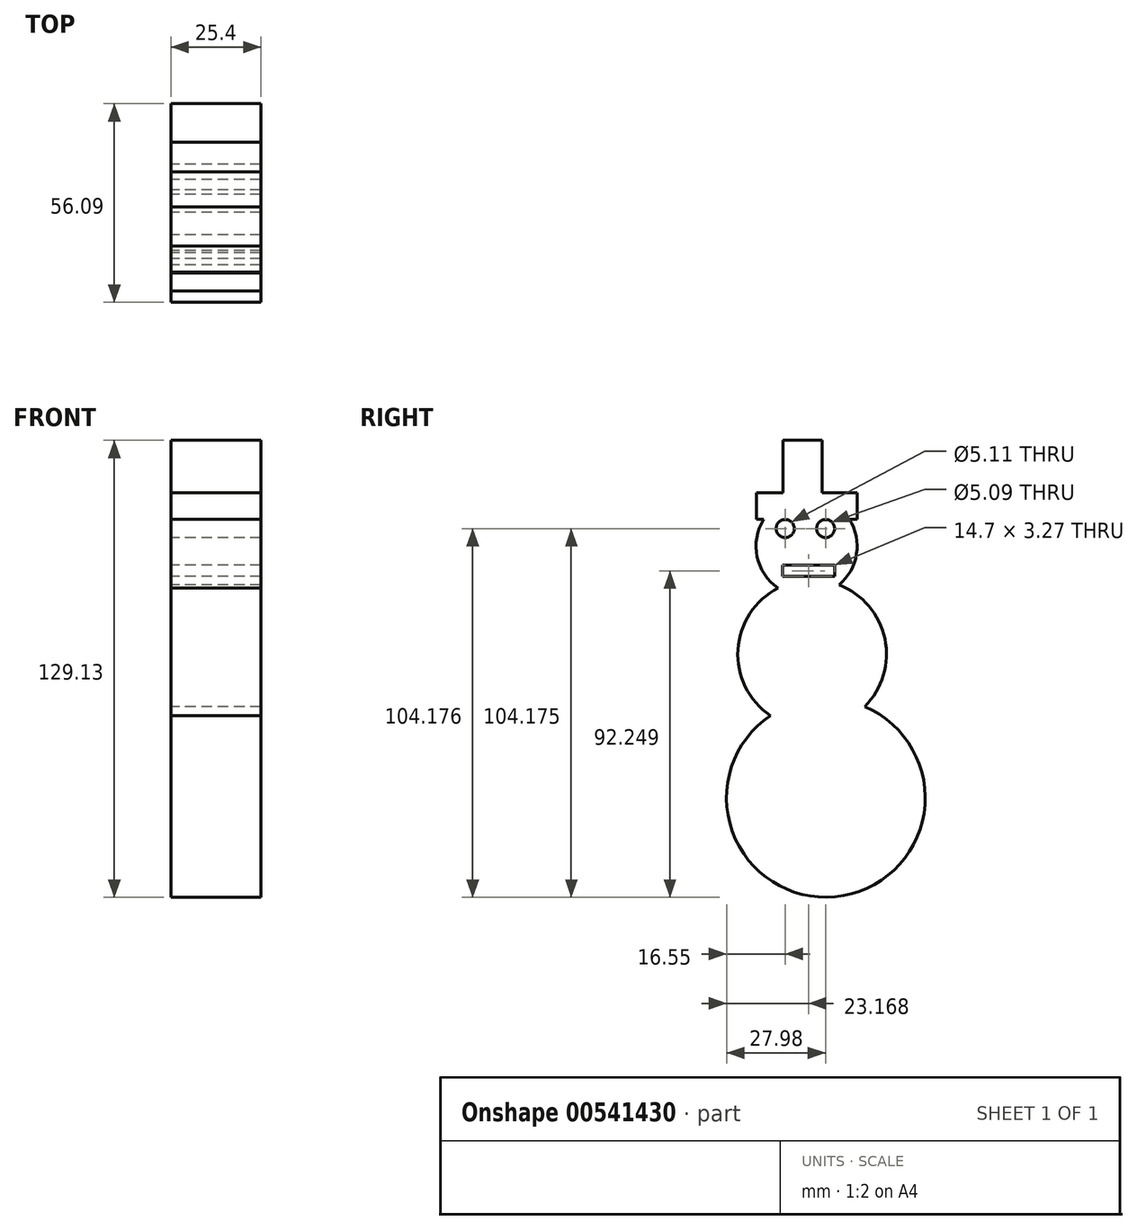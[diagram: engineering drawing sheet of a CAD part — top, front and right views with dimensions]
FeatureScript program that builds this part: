
annotation { "Feature Type Name" : "Feature", "Feature Type Description" : "" }
export const myFeature = defineFeature(function(context is Context, id is Id, definition is map)
    precondition{}
    {
        {
            var Q0;
            Q0=qCreatedBy(makeId("Right.planeOp"),FACE);
            var sketch = newSketch(context, id + "F0", { "sketchPlane" : qUnion([Q0])});
            skCircle(sketch, "E0", {"center": v(-8.83, -44.63) * mm, "radius": 28.05 * mm});
            skCircle(sketch, "E1", {"center": v(-12.7, -4) * mm, "radius": 21 * mm});
            skCircle(sketch, "E2", {"center": v(-14.27, 26.49) * mm, "radius": 14.27 * mm});
            skLineSegment(sketch, "E3.bottom", {"start": v(-28.42, 41.56) * mm, "end": v(0, 41.56) * mm});
            skLineSegment(sketch, "E3.top", {"start": v(-28.42, 34.1) * mm, "end": v(0, 34.1) * mm});
            skLineSegment(sketch, "E3.left", {"start": v(-28.42, 41.56) * mm, "end": v(-28.42, 34.1) * mm});
            skLineSegment(sketch, "E3.right", {"start": v(0, 41.56) * mm, "end": v(0, 34.1) * mm});
            skLineSegment(sketch, "E4.bottom", {"start": v(-20.97, 56.45) * mm, "end": v(-9.93, 56.45) * mm});
            skLineSegment(sketch, "E4.top", {"start": v(-20.97, 41.56) * mm, "end": v(-9.93, 41.56) * mm});
            skLineSegment(sketch, "E4.left", {"start": v(-20.97, 56.45) * mm, "end": v(-20.97, 41.56) * mm});
            skLineSegment(sketch, "E4.right", {"start": v(-9.93, 56.45) * mm, "end": v(-9.93, 41.56) * mm});
            skSolve(sketch);
        }
        {
            var Q0;
            Q0 = qSketchRegion(id + "F0", true);
            extrude(context, id + "F1", {"entities" : qUnion([Q0]), "depth" : 25.4 * mm, "offsetDistance" : 25.4 * mm});
        }
        {
            var Q0;
            Q0 = qSketchRegion(id + "F0", true);
            extrude(context, id + "F2", {"entities" : qUnion([Q0]), "operationType" : NewBodyOperationType.ADD, "depth" : 25.4 * mm, "offsetDistance" : 25.4 * mm});
        }
        {
            var Q0;
            Q0=qCreatedBy(makeId("Right.planeOp"),FACE);
            var sketch = newSketch(context, id + "F3", { "sketchPlane" : qUnion([Q0])});
            skCircle(sketch, "E5", {"center": v(-20.32, 31.5) * mm, "radius": 2.56 * mm});
            skCircle(sketch, "E6", {"center": v(-8.9, 31.5) * mm, "radius": 2.54 * mm});
            skLineSegment(sketch, "E7.bottom", {"start": v(-21.05, 21.2) * mm, "end": v(-6.35, 21.2) * mm});
            skLineSegment(sketch, "E7.top", {"start": v(-21.05, 17.94) * mm, "end": v(-6.35, 17.94) * mm});
            skLineSegment(sketch, "E7.left", {"start": v(-21.05, 21.2) * mm, "end": v(-21.05, 17.94) * mm});
            skLineSegment(sketch, "E7.right", {"start": v(-6.35, 21.2) * mm, "end": v(-6.35, 17.94) * mm});
            skSolve(sketch);
        }
        {
            var Q0;
            Q0 = qSketchRegion(id + "F3", true);
            extrude(context, id + "F4", {"entities" : qUnion([Q0]), "operationType" : NewBodyOperationType.REMOVE, "depth" : 25.4 * mm, "offsetDistance" : 25.4 * mm});
        }
        {
            var Q0;
            Q0=qCreatedBy(makeId("Right.planeOp"),FACE);
            var sketch = newSketch(context, id + "F5", { "sketchPlane" : qUnion([Q0])});
            skCircle(sketch, "E8", {"center": v(-14.59, 26.37) * mm, "radius": 1.78 * mm});
            skSolve(sketch);
        }
        {
            var Q0;
            Q0=sQuery(id+"F5.wireOp",EDGE,"E8");
            extrude(context, id + "F6", {"bodyType" : ToolBodyType.SURFACE, "surfaceEntities" : qUnion([Q0]), "depth" : 38.1 * mm, "offsetDistance" : 25.4 * mm});
        }
    });
